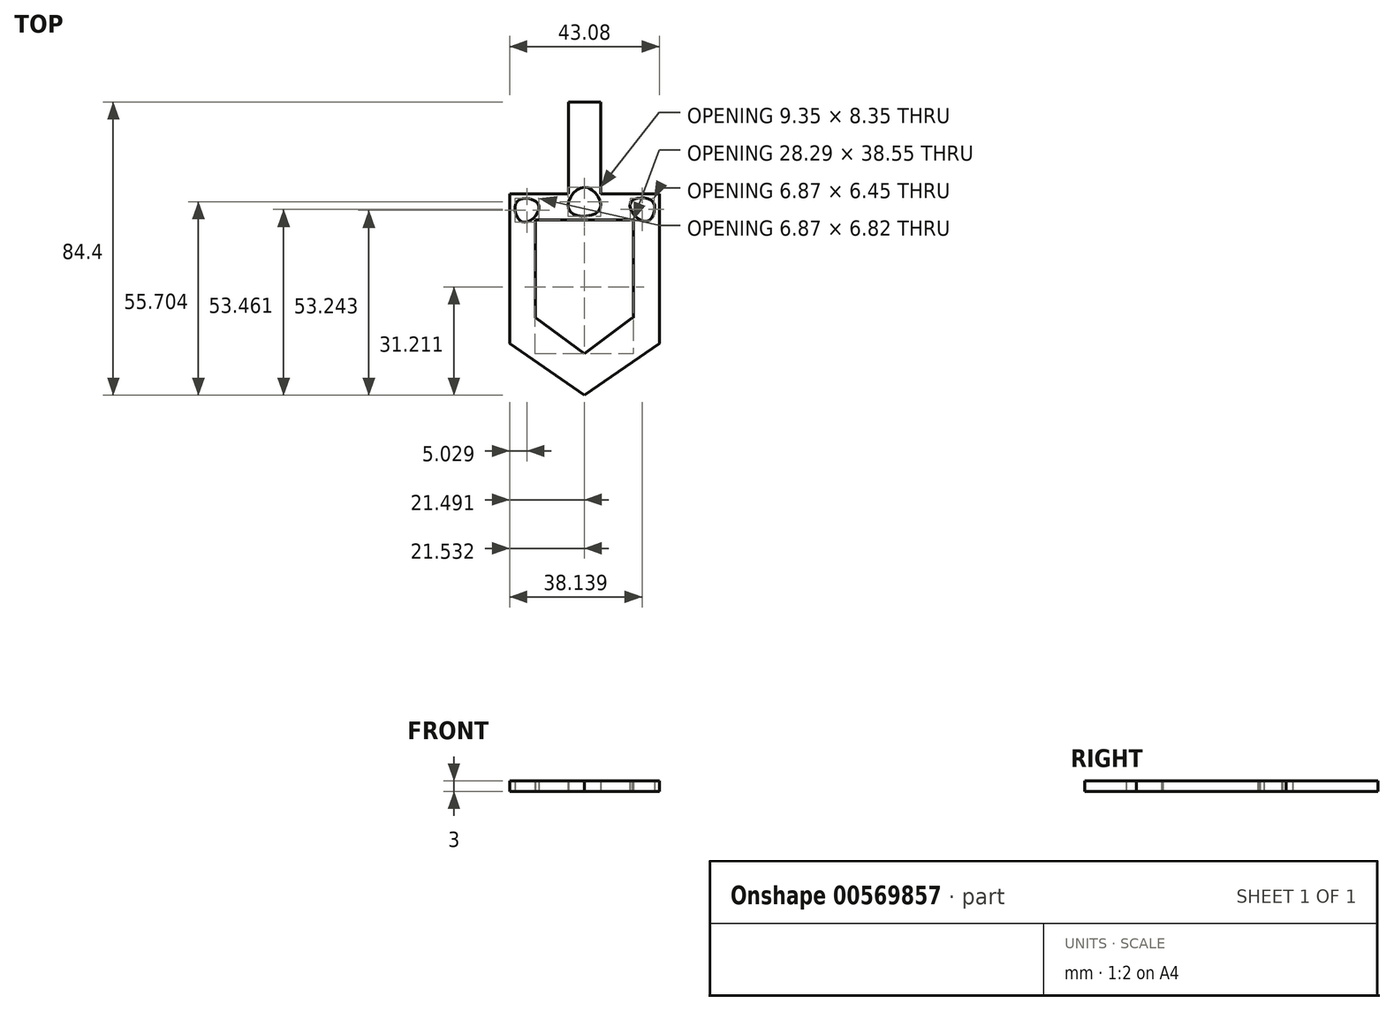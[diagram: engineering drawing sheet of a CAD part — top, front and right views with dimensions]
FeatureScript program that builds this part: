
annotation { "Feature Type Name" : "Feature", "Feature Type Description" : "" }
export const myFeature = defineFeature(function(context is Context, id is Id, definition is map)
    precondition{}
    {
        {
            var Q0;
            Q0=qCreatedBy(makeId("Top.planeOp"),FACE);
            var sketch = newSketch(context, id + "F0", { "sketchPlane" : qUnion([Q0])});
            skLineSegment(sketch, "E0.bottom", {"start": v(21.54, 21.54) * mm, "end": v(-21.54, 21.54) * mm});
            skLineSegment(sketch, "E0.top", {"start": v(21.54, -21.54) * mm, "end": v(-21.54, -21.54) * mm});
            skLineSegment(sketch, "E0.left", {"start": v(21.54, 21.54) * mm, "end": v(21.54, -21.54) * mm});
            skLineSegment(sketch, "E0.right", {"start": v(-21.54, 21.54) * mm, "end": v(-21.54, -21.54) * mm});
            skPoint(sketch, "E0.middle", {"position": v(0, 0) * mm});
            skLineSegment(sketch, "E1", {"start": v(-21.54, -21.54) * mm, "end": v(0, -36.4) * mm});
            skLineSegment(sketch, "E2", {"start": v(0, -36.4) * mm, "end": v(21.54, -21.54) * mm});
            skLineSegment(sketch, "E3.bottom", {"start": v(14.1, 14.1) * mm, "end": v(-14.1, 14.1) * mm});
            skLineSegment(sketch, "E3.top", {"start": v(14.1, -14.1) * mm, "end": v(-14.1, -14.1) * mm});
            skLineSegment(sketch, "E3.left", {"start": v(14.1, 14.1) * mm, "end": v(14.1, -14.1) * mm});
            skLineSegment(sketch, "E3.right", {"start": v(-14.1, 14.1) * mm, "end": v(-14.1, -14.1) * mm});
            skSolve(sketch);
        }
        {
            var Q0;
            Q0=makeQuery(id+"F0.imprint","IMPRINT",FACE,{"disambiguationData":[TD([[makeQuery(id+"F0.imprint","IMPRINT",EDGE,{"derivedFrom":sQuery(id+"F0.wireOp",EDGE,"E0.bottom")}),1.0]])]});
            extrude(context, id + "F1", {"entities" : qUnion([Q0]), "depth" : 3 * mm, "offsetDistance" : 25.4 * mm});
        }
        {
            var Q0;
            Q0=makeQuery(id+"F0.imprint","IMPRINT",FACE,{"disambiguationData":[TD([[makeQuery(id+"F0.imprint","IMPRINT",EDGE,{"derivedFrom":sQuery(id+"F0.wireOp",EDGE,"E0.top")}),1.0]])]});
            extrude(context, id + "F2", {"entities" : qUnion([Q0]), "operationType" : NewBodyOperationType.ADD, "depth" : 3 * mm, "offsetDistance" : 25.4 * mm});
        }
        {
            var Q0;
            Q0=qCreatedBy(makeId("Top.planeOp"),FACE);
            var sketch = newSketch(context, id + "F3", { "sketchPlane" : qUnion([Q0])});
            skLineSegment(sketch, "E4.bottom", {"start": v(4.65, 21.16) * mm, "end": v(-4.65, 21.16) * mm});
            skLineSegment(sketch, "E4.top", {"start": v(4.65, 48) * mm, "end": v(-4.65, 48) * mm});
            skLineSegment(sketch, "E4.left", {"start": v(4.65, 21.16) * mm, "end": v(4.65, 48) * mm});
            skLineSegment(sketch, "E4.right", {"start": v(-4.65, 21.16) * mm, "end": v(-4.65, 48) * mm});
            skPoint(sketch, "E4.middle", {"position": v(0, 34.58) * mm});
            skSolve(sketch);
        }
        {
            var Q0;
            Q0=makeQuery(id+"F3.imprint","IMPRINT",FACE,{"disambiguationData":[TD([[makeQuery(id+"F3.imprint","IMPRINT",EDGE,{"derivedFrom":sQuery(id+"F3.wireOp",EDGE,"E4.bottom")}),-1.0]])]});
            extrude(context, id + "F4", {"entities" : qUnion([Q0]), "operationType" : NewBodyOperationType.ADD, "depth" : 3 * mm, "offsetDistance" : 25.4 * mm});
        }
        {
            var Q0;
            Q0=qCreatedBy(makeId("Top.planeOp"),FACE);
            var sketch = newSketch(context, id + "F5", { "sketchPlane" : qUnion([Q0])});
            skLineSegment(sketch, "E5", {"start": v(-14.2, -13.94) * mm, "end": v(0, -24.45) * mm});
            skLineSegment(sketch, "E6", {"start": v(0, -24.45) * mm, "end": v(13.94, -13.94) * mm});
            skLineSegment(sketch, "E7", {"start": v(13.94, -13.94) * mm, "end": v(-14.2, -13.94) * mm});
            skSolve(sketch);
        }
        {
            var Q0;
            Q0=makeQuery(id+"F5.imprint","IMPRINT",FACE,{"disambiguationData":[TD([[makeQuery(id+"F5.imprint","IMPRINT",EDGE,{"derivedFrom":sQuery(id+"F5.wireOp",EDGE,"E5")}),1.0]])]});
            extrude(context, id + "F6", {"entities" : qUnion([Q0]), "operationType" : NewBodyOperationType.REMOVE, "depth" : 22.35 * mm, "offsetDistance" : 25.4 * mm});
        }
        {
            var Q0;
            Q0=qCreatedBy(makeId("Top.planeOp"),FACE);
            var sketch = newSketch(context, id + "F7", { "sketchPlane" : qUnion([Q0])});
            skFitSpline(sketch, "E8", {"points": [v(0, 23.49) * mm, v(-4.39, 16.78) * mm, v(4.39, 17.03) * mm, v(0, 23.49) * mm]});
            skFitSpline(sketch, "E9", {"points": [v(13.16, 18.84) * mm, v(19.62, 19.36) * mm, v(17.8, 13.68) * mm, v(13.16, 18.84) * mm]});
            skFitSpline(sketch, "E10", {"points": [v(-19.36, 19.36) * mm, v(-13.16, 18.32) * mm, v(-17.55, 13.42) * mm, v(-19.36, 19.36) * mm]});
            skSolve(sketch);
        }
        {
            var Q0;
            Q0=makeQuery(id+"F7.imprint","IMPRINT",FACE,{"disambiguationData":[TD([[makeQuery(id+"F7.imprint","IMPRINT",EDGE,{"derivedFrom":sQuery(id+"F7.wireOp",EDGE,"E8")}),1.0]])]});
            var Q1;
            Q1=makeQuery(id+"F7.imprint","IMPRINT",FACE,{"disambiguationData":[TD([[makeQuery(id+"F7.imprint","IMPRINT",EDGE,{"derivedFrom":sQuery(id+"F7.wireOp",EDGE,"E9")}),-1.0]])]});
            var Q2;
            Q2=makeQuery(id+"F7.imprint","IMPRINT",FACE,{"disambiguationData":[TD([[makeQuery(id+"F7.imprint","IMPRINT",EDGE,{"derivedFrom":sQuery(id+"F7.wireOp",EDGE,"E10")}),-1.0]])]});
            extrude(context, id + "F8", {"entities" : qUnion([Q0, Q1, Q2]), "operationType" : NewBodyOperationType.REMOVE, "depth" : 37.6 * mm, "offsetDistance" : 25.4 * mm});
        }
    });
